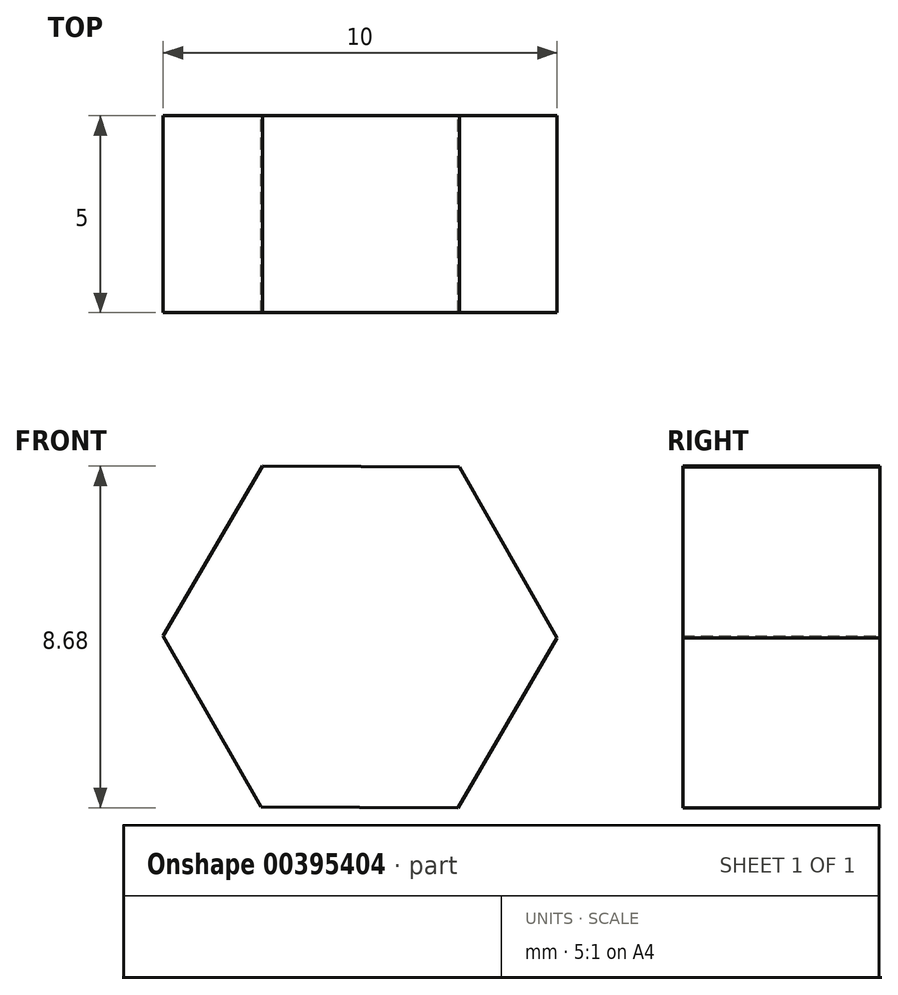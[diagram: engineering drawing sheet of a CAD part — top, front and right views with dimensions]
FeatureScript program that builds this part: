
annotation { "Feature Type Name" : "Feature", "Feature Type Description" : "" }
export const myFeature = defineFeature(function(context is Context, id is Id, definition is map)
    precondition{}
    {
        {
            var Q0;
            Q0=qCreatedBy(makeId("Front.planeOp"),FACE);
            var sketch = newSketch(context, id + "F0", { "sketchPlane" : qUnion([Q0])});
            skCircle(sketch, "E0.cCircle", {"center": v(0, 0) * mm, "radius": 4.33 * mm, "construction": true});
            skLineSegment(sketch, "E0.0", {"start": v(-2.52, -4.32) * mm, "end": v(-5, 0.02) * mm});
            skLineSegment(sketch, "E0.1", {"start": v(-5, 0.02) * mm, "end": v(-2.48, 4.34) * mm});
            skLineSegment(sketch, "E0.2", {"start": v(-2.48, 4.34) * mm, "end": v(2.52, 4.32) * mm});
            skLineSegment(sketch, "E0.3", {"start": v(2.52, 4.32) * mm, "end": v(5, -0.02) * mm});
            skLineSegment(sketch, "E0.4", {"start": v(5, -0.02) * mm, "end": v(2.48, -4.34) * mm});
            skLineSegment(sketch, "E0.5", {"start": v(2.48, -4.34) * mm, "end": v(-2.52, -4.32) * mm});
            skPoint(sketch, "E0.0.midPoint", {"position": v(-3.76, -2.15) * mm});
            skSolve(sketch);
        }
        {
            var Q0;
            Q0=makeQuery(id+"F0.imprint","IMPRINT",FACE,{"disambiguationData":[TD([[makeQuery(id+"F0.imprint","IMPRINT",EDGE,{"derivedFrom":sQuery(id+"F0.wireOp",EDGE,"E0.0")}),-1.0]])]});
            extrude(context, id + "F1", {"entities" : qUnion([Q0]), "depth" : 5 * mm});
        }
    });
